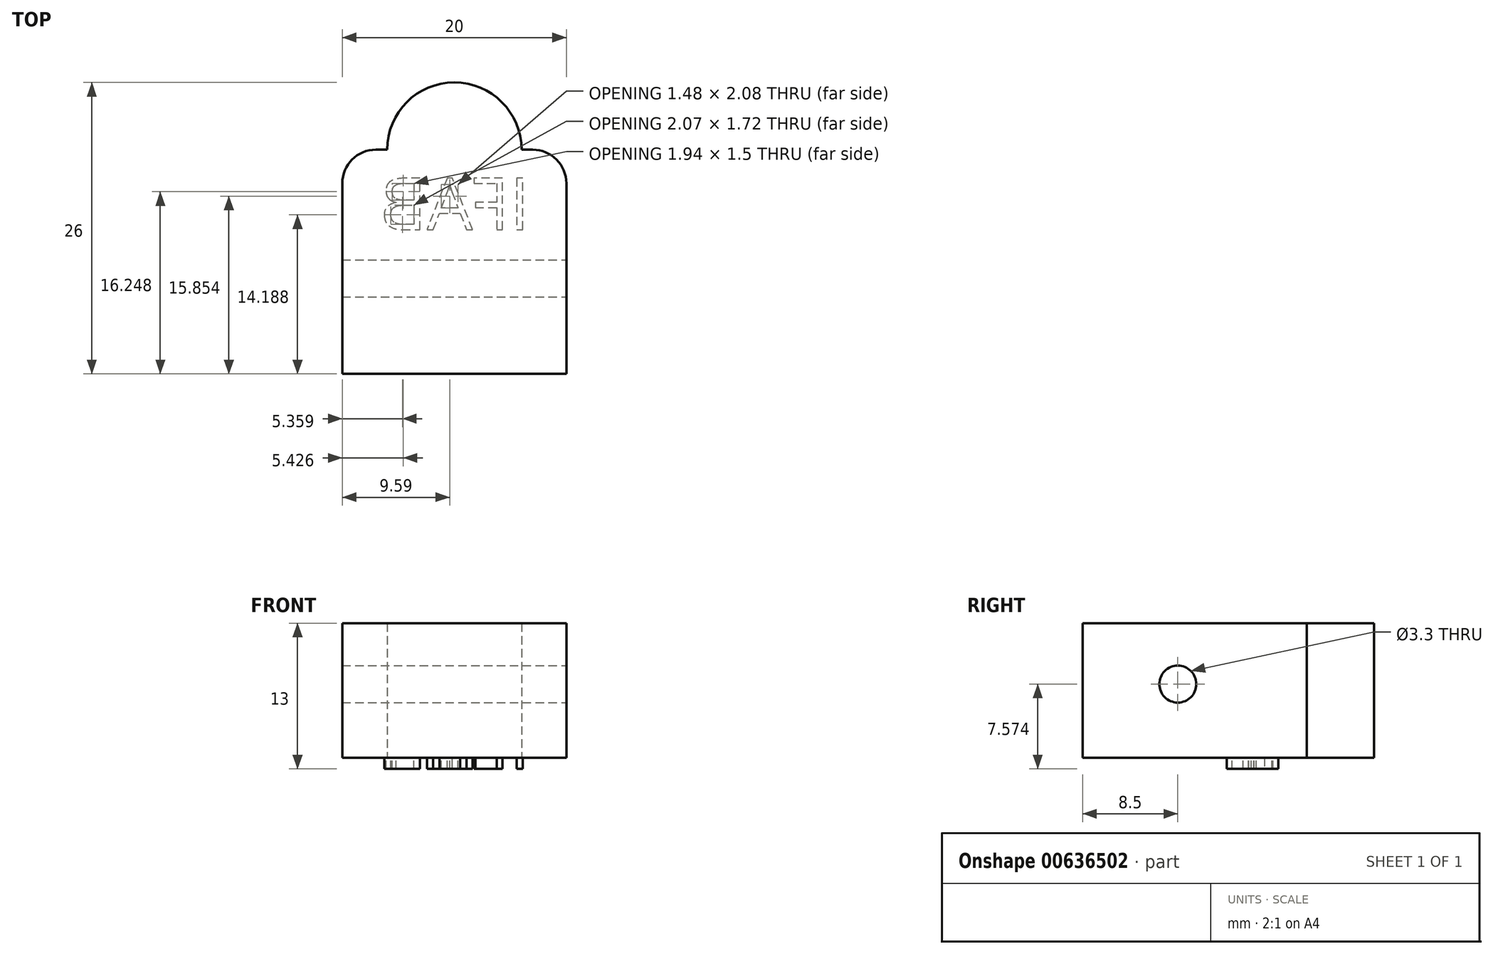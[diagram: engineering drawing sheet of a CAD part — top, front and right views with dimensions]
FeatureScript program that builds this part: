
annotation { "Feature Type Name" : "Feature", "Feature Type Description" : "" }
export const myFeature = defineFeature(function(context is Context, id is Id, definition is map)
    precondition{}
    {
        {
            var Q0;
            Q0=qCreatedBy(makeId("Top.planeOp"),FACE);
            var sketch = newSketch(context, id + "F0", { "sketchPlane" : qUnion([Q0])});
            skCircle(sketch, "E0", {"center": v(0, 0) * mm, "radius": 6 * mm});
            skLineSegment(sketch, "E1.bottom", {"start": v(-10, 0) * mm, "end": v(10, 0) * mm});
            skLineSegment(sketch, "E1.top", {"start": v(-10, -20) * mm, "end": v(10, -20) * mm});
            skLineSegment(sketch, "E1.left", {"start": v(-10, 0) * mm, "end": v(-10, -20) * mm});
            skLineSegment(sketch, "E1.right", {"start": v(10, 0) * mm, "end": v(10, -20) * mm});
            skSolve(sketch);
        }
        {
            var Q0;
            Q0=makeQuery(id+"F0.imprint","IMPRINT",FACE,{"disambiguationData":[TD([[makeQuery(id+"F0.imprint","IMPRINT",EDGE,{"derivedFrom":sQuery(id+"F0.wireOp",EDGE,"E1.top")}),1.0]])]});
            var Q1;
            {var subQ0=sQuery(id+"F0.wireOp",EDGE,"E1.bottom");var subQ1=sQuery(id+"F0.wireOp",EDGE,"E0");var subQ2=makeQuery(id+"F0.imprint","INTERSECT",VERTEX,{"disambiguationData":[OD(0.0)],"derivedFrom":[subQ1,subQ0]});Q1=makeQuery(id+"F0.imprint","IMPRINT",FACE,{"disambiguationData":[TD([[makeQuery(id+"F0.imprint","IMPRINT",EDGE,{"disambiguationData":[TD([[subQ2,-1.0]])],"derivedFrom":subQ1}),1.0]])]});}
            var Q2;
            {var subQ0=sQuery(id+"F0.wireOp",EDGE,"E1.bottom");var subQ1=sQuery(id+"F0.wireOp",EDGE,"E0");var subQ2=makeQuery(id+"F0.imprint","INTERSECT",VERTEX,{"disambiguationData":[OD(0.0)],"derivedFrom":[subQ1,subQ0]});Q2=makeQuery(id+"F0.imprint","IMPRINT",FACE,{"disambiguationData":[TD([[makeQuery(id+"F0.imprint","IMPRINT",EDGE,{"disambiguationData":[TD([[subQ2,1.0]])],"derivedFrom":subQ1}),1.0]])]});}
            extrude(context, id + "F1", {"entities" : qUnion([Q0, Q1, Q2]), "depth" : 12 * mm, "offsetDistance" : 25 * mm});
        }
        {
            var Q0;
            Q0=makeQuery(id+"F1.opExtrude","SWEPT_EDGE",EDGE,{"disambiguationData":[OSD([sQuery(id+"F0.wireOp",EDGE,"E1.bottom"),sQuery(id+"F0.wireOp",EDGE,"E1.left")])]});
            var Q1;
            Q1=makeQuery(id+"F1.opExtrude","SWEPT_EDGE",EDGE,{"disambiguationData":[OSD([sQuery(id+"F0.wireOp",EDGE,"E1.bottom"),sQuery(id+"F0.wireOp",EDGE,"E1.right")])]});
            fillet(context, id + "F2", {"entities" : qUnion([Q0, Q1]), "radius" : 3 * mm, "tangentPropagation" : true, "allowEdgeOverflow" : false});
        }
        {
            var Q0;
            Q0=makeQuery(id+"F1.opExtrude","SWEPT_FACE",FACE,{"disambiguationData":[OSD([sQuery(id+"F0.wireOp",EDGE,"E1.right")])]});
            var sketch = newSketch(context, id + "F3", { "sketchPlane" : qUnion([Q0])});
            skPoint(sketch, "E2", {"position": v(-11.5, 6.57) * mm});
            skPoint(sketch, "E2.positionSnap0", {"position": v(-11.5, 12) * mm});
            skSolve(sketch);
        }
        {
            var Q0;
            Q0=sQuery(id+"F3.wireOp",VERTEX,"E2");
            var Q1;
            Q1=makeQuery(id+"F1.opExtrude","SWEPT_BODY",BODY,{"disambiguationData":[OSD([sQuery(id+"F0.wireOp",EDGE,"E0"),sQuery(id+"F0.wireOp",EDGE,"E1.bottom"),sQuery(id+"F0.wireOp",EDGE,"E1.top"),sQuery(id+"F0.wireOp",EDGE,"E1.left"),sQuery(id+"F0.wireOp",EDGE,"E1.right")])]});
            hole(context, id + "F4", {"style" : HoleStyle.SIMPLE, "endStyle" : HoleEndStyle.BLIND, "standardTappedOrClearance" : lookupTablePath({ "standard" : "ISO", "fit" : "Normal", "size" : "M3", "type" : "Clearance" }), "standardBlindInLast" : lookupTablePath({ "fit" : "Standard", "standard" : "ISO", "size" : "M3", "type" : "Clearance" }), "holeDiameter" : 3.3 * mm, "majorDiameter" : 5 * mm, "holeDepth" : 30 * mm, "isTappedThrough" : true, "tappedDepth" : 12 * mm, "tapClearance" : 3, "locations" : qUnion([Q0]), "scope" : qUnion([Q1])});
        }
        {
            var Q0;
            Q0=makeQuery(id+"F1.opExtrude","CAP_FACE",FACE,{"disambiguationData":[OSD([sQuery(id+"F0.wireOp",EDGE,"E0"),sQuery(id+"F0.wireOp",EDGE,"E1.bottom"),sQuery(id+"F0.wireOp",EDGE,"E1.top"),sQuery(id+"F0.wireOp",EDGE,"E1.left"),sQuery(id+"F0.wireOp",EDGE,"E1.right")])],"isStart":true});
            var sketch = newSketch(context, id + "F5", { "sketchPlane" : qUnion([Q0])});
            skText(sketch, "E3", { "text": "IFAB", "fontName": "OpenSans-Regular.ttf"});
            const initialGuessF5  = {"E3": [-0.01346, 0.00575, 1, 0, 0.00925]};
            skSetInitialGuess(sketch, initialGuessF5);
            skSolve(sketch);
        }
        {
            var Q0;
            Q0 = qSketchRegion(id + "F5", true);
            extrude(context, id + "F6", {"entities" : qUnion([Q0]), "depth" : 2 * mm, "offsetDistance" : 25 * mm});
        }
        {
            var Q0;
            Q0=makeQuery(id+"F6.opExtrude","SWEPT_BODY",BODY,{"disambiguationData":[OSD([sQuery(id+"F5.wireOp",EDGE,"E3.sketch_text.stroke-0"),sQuery(id+"F5.wireOp",EDGE,"E3.sketch_text.stroke-1"),sQuery(id+"F5.wireOp",EDGE,"E3.sketch_text.stroke-2"),sQuery(id+"F5.wireOp",EDGE,"E3.sketch_text.stroke-3")])]});
            var Q1;
            Q1=makeQuery(id+"F6.opExtrude","SWEPT_BODY",BODY,{"disambiguationData":[OSD([sQuery(id+"F5.wireOp",EDGE,"E3.sketch_text.stroke-4"),sQuery(id+"F5.wireOp",EDGE,"E3.sketch_text.stroke-5"),sQuery(id+"F5.wireOp",EDGE,"E3.sketch_text.stroke-6"),sQuery(id+"F5.wireOp",EDGE,"E3.sketch_text.stroke-7"),sQuery(id+"F5.wireOp",EDGE,"E3.sketch_text.stroke-8"),sQuery(id+"F5.wireOp",EDGE,"E3.sketch_text.stroke-9"),sQuery(id+"F5.wireOp",EDGE,"E3.sketch_text.stroke-10"),sQuery(id+"F5.wireOp",EDGE,"E3.sketch_text.stroke-11"),sQuery(id+"F5.wireOp",EDGE,"E3.sketch_text.stroke-12"),sQuery(id+"F5.wireOp",EDGE,"E3.sketch_text.stroke-13")])]});
            var Q2;
            Q2=makeQuery(id+"F6.opExtrude","SWEPT_BODY",BODY,{"disambiguationData":[OSD([sQuery(id+"F5.wireOp",EDGE,"E3.sketch_text.stroke-14"),sQuery(id+"F5.wireOp",EDGE,"E3.sketch_text.stroke-15"),sQuery(id+"F5.wireOp",EDGE,"E3.sketch_text.stroke-16"),sQuery(id+"F5.wireOp",EDGE,"E3.sketch_text.stroke-17"),sQuery(id+"F5.wireOp",EDGE,"E3.sketch_text.stroke-18"),sQuery(id+"F5.wireOp",EDGE,"E3.sketch_text.stroke-19"),sQuery(id+"F5.wireOp",EDGE,"E3.sketch_text.stroke-20"),sQuery(id+"F5.wireOp",EDGE,"E3.sketch_text.stroke-21"),sQuery(id+"F5.wireOp",EDGE,"E3.sketch_text.stroke-22"),sQuery(id+"F5.wireOp",EDGE,"E3.sketch_text.stroke-23"),sQuery(id+"F5.wireOp",EDGE,"E3.sketch_text.stroke-24"),sQuery(id+"F5.wireOp",EDGE,"E3.sketch_text.stroke-25"),sQuery(id+"F5.wireOp",EDGE,"E3.sketch_text.stroke-26")])]});
            var Q3;
            Q3=makeQuery(id+"F6.opExtrude","SWEPT_BODY",BODY,{"disambiguationData":[OSD([sQuery(id+"F5.wireOp",EDGE,"E3.sketch_text.stroke-27"),sQuery(id+"F5.wireOp",EDGE,"E3.sketch_text.stroke-28"),sQuery(id+"F5.wireOp",EDGE,"E3.sketch_text.stroke-29"),sQuery(id+"F5.wireOp",EDGE,"E3.sketch_text.stroke-30"),sQuery(id+"F5.wireOp",EDGE,"E3.sketch_text.stroke-31"),sQuery(id+"F5.wireOp",EDGE,"E3.sketch_text.stroke-32"),sQuery(id+"F5.wireOp",EDGE,"E3.sketch_text.stroke-33"),sQuery(id+"F5.wireOp",EDGE,"E3.sketch_text.stroke-34"),sQuery(id+"F5.wireOp",EDGE,"E3.sketch_text.stroke-35"),sQuery(id+"F5.wireOp",EDGE,"E3.sketch_text.stroke-36"),sQuery(id+"F5.wireOp",EDGE,"E3.sketch_text.stroke-37"),sQuery(id+"F5.wireOp",EDGE,"E3.sketch_text.stroke-38"),sQuery(id+"F5.wireOp",EDGE,"E3.sketch_text.stroke-39"),sQuery(id+"F5.wireOp",EDGE,"E3.sketch_text.stroke-40"),sQuery(id+"F5.wireOp",EDGE,"E3.sketch_text.stroke-41"),sQuery(id+"F5.wireOp",EDGE,"E3.sketch_text.stroke-42"),sQuery(id+"F5.wireOp",EDGE,"E3.sketch_text.stroke-43"),sQuery(id+"F5.wireOp",EDGE,"E3.sketch_text.stroke-44"),sQuery(id+"F5.wireOp",EDGE,"E3.sketch_text.stroke-45"),sQuery(id+"F5.wireOp",EDGE,"E3.sketch_text.stroke-46"),sQuery(id+"F5.wireOp",EDGE,"E3.sketch_text.stroke-47"),sQuery(id+"F5.wireOp",EDGE,"E3.sketch_text.stroke-48"),sQuery(id+"F5.wireOp",EDGE,"E3.sketch_text.stroke-49"),sQuery(id+"F5.wireOp",EDGE,"E3.sketch_text.stroke-50"),sQuery(id+"F5.wireOp",EDGE,"E3.sketch_text.stroke-51")])]});
            var Q4;
            Q4=qCreatedBy(makeId("Origin.pointOp"),VERTEX);
            transform(context, id + "F7", {"entities" : qUnion([Q0, Q1, Q2, Q3]), "transformType" : TransformType.SCALE_UNIFORMLY, "scale" : 0.5, "scalePoint" : qUnion([Q4]), "makeCopy" : false});
        }
        {
            var Q0;
            Q0=qCreatedBy(makeId("Front.planeOp"),FACE);
            var sketch = newSketch(context, id + "F8", { "sketchPlane" : qUnion([Q0])});
            skLineSegment(sketch, "E4", {"start": v(0, 0) * mm, "end": v(0, 17.23) * mm, "construction": true});
            skSolve(sketch);
        }
        {
            var Q0;
            Q0=makeQuery(id+"F6.opExtrude","SWEPT_BODY",BODY,{"disambiguationData":[OSD([sQuery(id+"F5.wireOp",EDGE,"E3.sketch_text.stroke-0"),sQuery(id+"F5.wireOp",EDGE,"E3.sketch_text.stroke-1"),sQuery(id+"F5.wireOp",EDGE,"E3.sketch_text.stroke-2"),sQuery(id+"F5.wireOp",EDGE,"E3.sketch_text.stroke-3")])]});
            var Q1;
            Q1=makeQuery(id+"F6.opExtrude","SWEPT_BODY",BODY,{"disambiguationData":[OSD([sQuery(id+"F5.wireOp",EDGE,"E3.sketch_text.stroke-4"),sQuery(id+"F5.wireOp",EDGE,"E3.sketch_text.stroke-5"),sQuery(id+"F5.wireOp",EDGE,"E3.sketch_text.stroke-6"),sQuery(id+"F5.wireOp",EDGE,"E3.sketch_text.stroke-7"),sQuery(id+"F5.wireOp",EDGE,"E3.sketch_text.stroke-8"),sQuery(id+"F5.wireOp",EDGE,"E3.sketch_text.stroke-9"),sQuery(id+"F5.wireOp",EDGE,"E3.sketch_text.stroke-10"),sQuery(id+"F5.wireOp",EDGE,"E3.sketch_text.stroke-11"),sQuery(id+"F5.wireOp",EDGE,"E3.sketch_text.stroke-12"),sQuery(id+"F5.wireOp",EDGE,"E3.sketch_text.stroke-13")])]});
            var Q2;
            Q2=makeQuery(id+"F6.opExtrude","SWEPT_BODY",BODY,{"disambiguationData":[OSD([sQuery(id+"F5.wireOp",EDGE,"E3.sketch_text.stroke-14"),sQuery(id+"F5.wireOp",EDGE,"E3.sketch_text.stroke-15"),sQuery(id+"F5.wireOp",EDGE,"E3.sketch_text.stroke-16"),sQuery(id+"F5.wireOp",EDGE,"E3.sketch_text.stroke-17"),sQuery(id+"F5.wireOp",EDGE,"E3.sketch_text.stroke-18"),sQuery(id+"F5.wireOp",EDGE,"E3.sketch_text.stroke-19"),sQuery(id+"F5.wireOp",EDGE,"E3.sketch_text.stroke-20"),sQuery(id+"F5.wireOp",EDGE,"E3.sketch_text.stroke-21"),sQuery(id+"F5.wireOp",EDGE,"E3.sketch_text.stroke-22"),sQuery(id+"F5.wireOp",EDGE,"E3.sketch_text.stroke-23"),sQuery(id+"F5.wireOp",EDGE,"E3.sketch_text.stroke-24"),sQuery(id+"F5.wireOp",EDGE,"E3.sketch_text.stroke-25"),sQuery(id+"F5.wireOp",EDGE,"E3.sketch_text.stroke-26")])]});
            var Q3;
            Q3=makeQuery(id+"F6.opExtrude","SWEPT_BODY",BODY,{"disambiguationData":[OSD([sQuery(id+"F5.wireOp",EDGE,"E3.sketch_text.stroke-27"),sQuery(id+"F5.wireOp",EDGE,"E3.sketch_text.stroke-28"),sQuery(id+"F5.wireOp",EDGE,"E3.sketch_text.stroke-29"),sQuery(id+"F5.wireOp",EDGE,"E3.sketch_text.stroke-30"),sQuery(id+"F5.wireOp",EDGE,"E3.sketch_text.stroke-31"),sQuery(id+"F5.wireOp",EDGE,"E3.sketch_text.stroke-32"),sQuery(id+"F5.wireOp",EDGE,"E3.sketch_text.stroke-33"),sQuery(id+"F5.wireOp",EDGE,"E3.sketch_text.stroke-34"),sQuery(id+"F5.wireOp",EDGE,"E3.sketch_text.stroke-35"),sQuery(id+"F5.wireOp",EDGE,"E3.sketch_text.stroke-36"),sQuery(id+"F5.wireOp",EDGE,"E3.sketch_text.stroke-37"),sQuery(id+"F5.wireOp",EDGE,"E3.sketch_text.stroke-38"),sQuery(id+"F5.wireOp",EDGE,"E3.sketch_text.stroke-39"),sQuery(id+"F5.wireOp",EDGE,"E3.sketch_text.stroke-40"),sQuery(id+"F5.wireOp",EDGE,"E3.sketch_text.stroke-41"),sQuery(id+"F5.wireOp",EDGE,"E3.sketch_text.stroke-42"),sQuery(id+"F5.wireOp",EDGE,"E3.sketch_text.stroke-43"),sQuery(id+"F5.wireOp",EDGE,"E3.sketch_text.stroke-44"),sQuery(id+"F5.wireOp",EDGE,"E3.sketch_text.stroke-45"),sQuery(id+"F5.wireOp",EDGE,"E3.sketch_text.stroke-46"),sQuery(id+"F5.wireOp",EDGE,"E3.sketch_text.stroke-47"),sQuery(id+"F5.wireOp",EDGE,"E3.sketch_text.stroke-48"),sQuery(id+"F5.wireOp",EDGE,"E3.sketch_text.stroke-49"),sQuery(id+"F5.wireOp",EDGE,"E3.sketch_text.stroke-50"),sQuery(id+"F5.wireOp",EDGE,"E3.sketch_text.stroke-51")])]});
            var Q4;
            Q4=sQuery(id+"F8.wireOp",EDGE,"E4");
            transform(context, id + "F9", {"entities" : qUnion([Q0, Q1, Q2, Q3]), "transformType" : TransformType.ROTATION, "transformAxis" : qUnion([Q4]), "angle" : 180 * degree, "makeCopy" : false});
        }
        {
            var Q0;
            Q0=makeQuery(id+"F6.opExtrude","SWEPT_BODY",BODY,{"disambiguationData":[OSD([sQuery(id+"F5.wireOp",EDGE,"E3.sketch_text.stroke-0"),sQuery(id+"F5.wireOp",EDGE,"E3.sketch_text.stroke-1"),sQuery(id+"F5.wireOp",EDGE,"E3.sketch_text.stroke-2"),sQuery(id+"F5.wireOp",EDGE,"E3.sketch_text.stroke-3")])]});
            var Q1;
            Q1=makeQuery(id+"F6.opExtrude","SWEPT_BODY",BODY,{"disambiguationData":[OSD([sQuery(id+"F5.wireOp",EDGE,"E3.sketch_text.stroke-4"),sQuery(id+"F5.wireOp",EDGE,"E3.sketch_text.stroke-5"),sQuery(id+"F5.wireOp",EDGE,"E3.sketch_text.stroke-6"),sQuery(id+"F5.wireOp",EDGE,"E3.sketch_text.stroke-7"),sQuery(id+"F5.wireOp",EDGE,"E3.sketch_text.stroke-8"),sQuery(id+"F5.wireOp",EDGE,"E3.sketch_text.stroke-9"),sQuery(id+"F5.wireOp",EDGE,"E3.sketch_text.stroke-10"),sQuery(id+"F5.wireOp",EDGE,"E3.sketch_text.stroke-11"),sQuery(id+"F5.wireOp",EDGE,"E3.sketch_text.stroke-12"),sQuery(id+"F5.wireOp",EDGE,"E3.sketch_text.stroke-13")])]});
            var Q2;
            Q2=makeQuery(id+"F6.opExtrude","SWEPT_BODY",BODY,{"disambiguationData":[OSD([sQuery(id+"F5.wireOp",EDGE,"E3.sketch_text.stroke-14"),sQuery(id+"F5.wireOp",EDGE,"E3.sketch_text.stroke-15"),sQuery(id+"F5.wireOp",EDGE,"E3.sketch_text.stroke-16"),sQuery(id+"F5.wireOp",EDGE,"E3.sketch_text.stroke-17"),sQuery(id+"F5.wireOp",EDGE,"E3.sketch_text.stroke-18"),sQuery(id+"F5.wireOp",EDGE,"E3.sketch_text.stroke-19"),sQuery(id+"F5.wireOp",EDGE,"E3.sketch_text.stroke-20"),sQuery(id+"F5.wireOp",EDGE,"E3.sketch_text.stroke-21"),sQuery(id+"F5.wireOp",EDGE,"E3.sketch_text.stroke-22"),sQuery(id+"F5.wireOp",EDGE,"E3.sketch_text.stroke-23"),sQuery(id+"F5.wireOp",EDGE,"E3.sketch_text.stroke-24"),sQuery(id+"F5.wireOp",EDGE,"E3.sketch_text.stroke-25"),sQuery(id+"F5.wireOp",EDGE,"E3.sketch_text.stroke-26")])]});
            var Q3;
            Q3=makeQuery(id+"F6.opExtrude","SWEPT_BODY",BODY,{"disambiguationData":[OSD([sQuery(id+"F5.wireOp",EDGE,"E3.sketch_text.stroke-27"),sQuery(id+"F5.wireOp",EDGE,"E3.sketch_text.stroke-28"),sQuery(id+"F5.wireOp",EDGE,"E3.sketch_text.stroke-29"),sQuery(id+"F5.wireOp",EDGE,"E3.sketch_text.stroke-30"),sQuery(id+"F5.wireOp",EDGE,"E3.sketch_text.stroke-31"),sQuery(id+"F5.wireOp",EDGE,"E3.sketch_text.stroke-32"),sQuery(id+"F5.wireOp",EDGE,"E3.sketch_text.stroke-33"),sQuery(id+"F5.wireOp",EDGE,"E3.sketch_text.stroke-34"),sQuery(id+"F5.wireOp",EDGE,"E3.sketch_text.stroke-35"),sQuery(id+"F5.wireOp",EDGE,"E3.sketch_text.stroke-36"),sQuery(id+"F5.wireOp",EDGE,"E3.sketch_text.stroke-37"),sQuery(id+"F5.wireOp",EDGE,"E3.sketch_text.stroke-38"),sQuery(id+"F5.wireOp",EDGE,"E3.sketch_text.stroke-39"),sQuery(id+"F5.wireOp",EDGE,"E3.sketch_text.stroke-40"),sQuery(id+"F5.wireOp",EDGE,"E3.sketch_text.stroke-41"),sQuery(id+"F5.wireOp",EDGE,"E3.sketch_text.stroke-42"),sQuery(id+"F5.wireOp",EDGE,"E3.sketch_text.stroke-43"),sQuery(id+"F5.wireOp",EDGE,"E3.sketch_text.stroke-44"),sQuery(id+"F5.wireOp",EDGE,"E3.sketch_text.stroke-45"),sQuery(id+"F5.wireOp",EDGE,"E3.sketch_text.stroke-46"),sQuery(id+"F5.wireOp",EDGE,"E3.sketch_text.stroke-47"),sQuery(id+"F5.wireOp",EDGE,"E3.sketch_text.stroke-48"),sQuery(id+"F5.wireOp",EDGE,"E3.sketch_text.stroke-49"),sQuery(id+"F5.wireOp",EDGE,"E3.sketch_text.stroke-50"),sQuery(id+"F5.wireOp",EDGE,"E3.sketch_text.stroke-51")])]});
            var Q4;
            Q4=makeQuery(id+"F1.opExtrude","CAP_EDGE",EDGE,{"disambiguationData":[OSD([sQuery(id+"F0.wireOp",EDGE,"E1.left")])],"isStart":true});
            transform(context, id + "F10", {"entities" : qUnion([Q0, Q1, Q2, Q3]), "transformType" : TransformType.TRANSLATION_DISTANCE, "transformDirection" : qUnion([Q4]), "distance" : 10 * mm, "makeCopy" : false});
        }
    });
